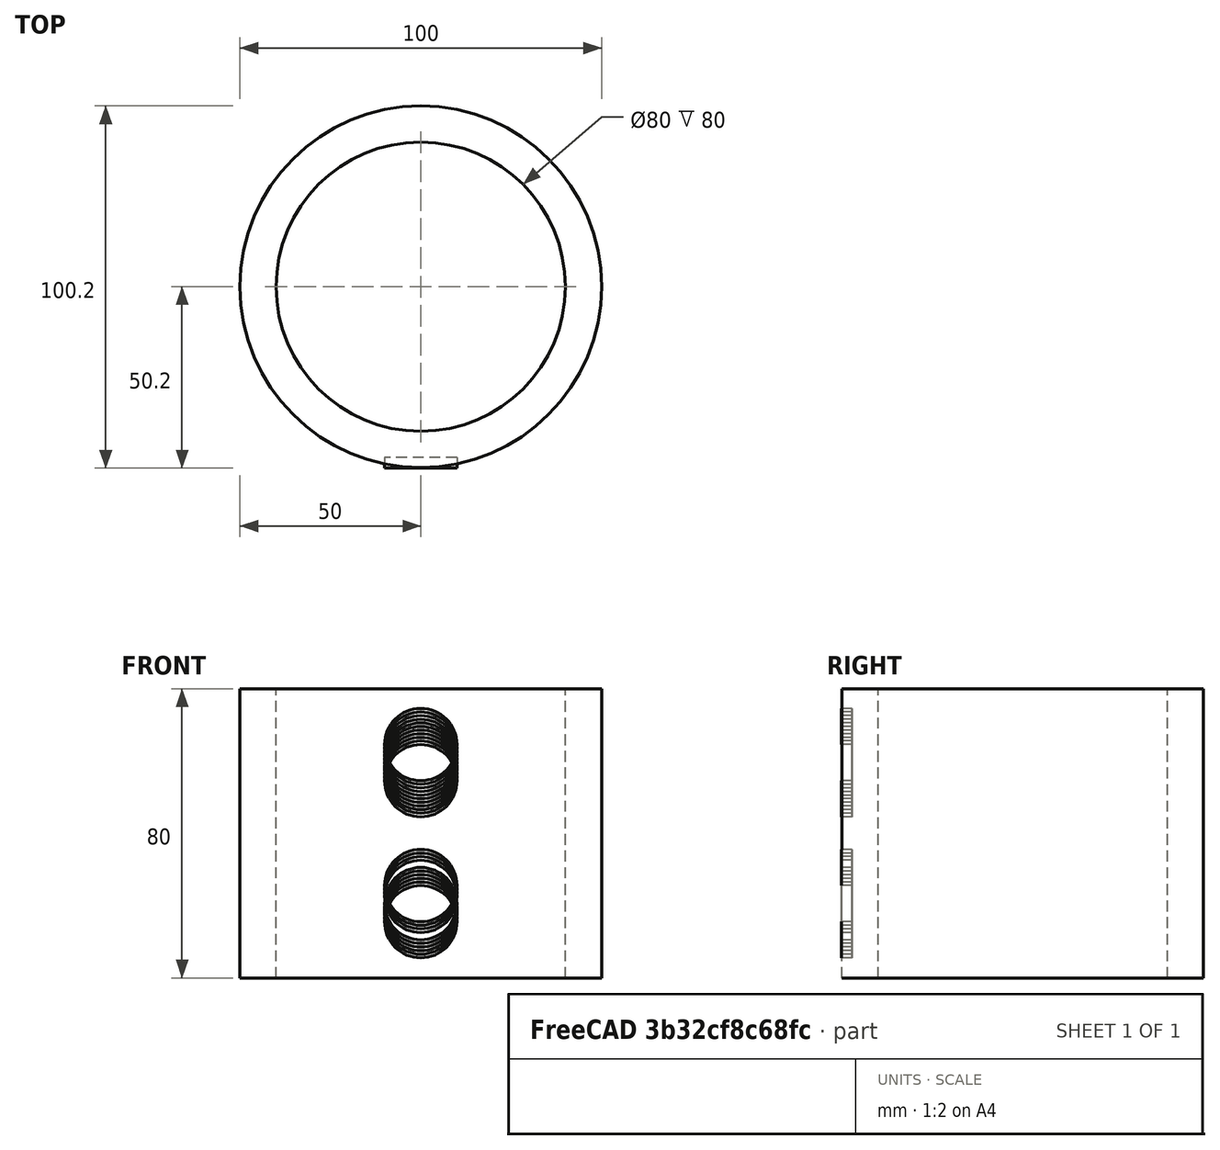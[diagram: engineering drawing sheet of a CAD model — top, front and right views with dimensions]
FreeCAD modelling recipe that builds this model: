
FCSTD DOCUMENT  (FreeCAD 0.18R16146 (Git))
Label: energy-free
License: All rights reserved
LicenseURL: http://en.wikipedia.org/wiki/All_rights_reserved
objects: Part::Cylinder×26, App::Part×13, Part::Cut×1
note: 27 computed .brp shape members not serialized (recipe doc carries the construction recipe); baked Part::Feature solids carry a one-line shape summary decoded from their .brp

FEATURE [Part::Cylinder] Cylinder  label="cercle  externe"
  Angle = 360
  AttacherType = Attacher::AttachEngine3D
  Height = 80
  Radius = 50
FEATURE [Part::Cylinder] Cylinder001  label="cercle interne"
  Angle = 360
  AttacherType = Attacher::AttachEngine3D
  Height = 80
  Radius = 40
FEATURE [Part::Cut] Cut
  Base = -> Cylinder
  Tool = -> Cylinder001
FEATURE [App::Part] Part
  Group = -> [Cylinder,Cylinder001,Cut]
  Origin = -> Origin
FEATURE [Part::Cylinder] Cylinder004  label="Cylindre004"
  Angle = 360
  AttacherType = Attacher::AttachEngine3D
  Height = 3
  Placement = pos=(0,-47.2044,15.5529) rot=(1,0,0;1.5708rad)
  Radius = 10
FEATURE [Part::Cylinder] Cylinder006  label="Cylindre006"
  Angle = 360
  AttacherType = Attacher::AttachEngine3D
  Height = 3
  Placement = pos=(0,-47.2044,64.5529) rot=(1,0,0;1.5708rad)
  Radius = 10
FEATURE [App::Part] Part001
  Group = -> [Cylinder004,Cylinder006]
  Origin = -> Origin001
  Placement = pos=(0,0,0) rot=(0,0,1;0.523599rad)
FEATURE [Part::Cylinder] Cylinder007  label="Cylindre007"
  Angle = 360
  AttacherType = Attacher::AttachEngine3D
  Height = 3
  Placement = pos=(0,-47.2044,16.5529) rot=(1,0,0;1.5708rad)
  Radius = 10
FEATURE [Part::Cylinder] Cylinder008  label="Cylindre008"
  Angle = 360
  AttacherType = Attacher::AttachEngine3D
  Height = 3
  Placement = pos=(0,-47.2044,63.5529) rot=(1,0,0;1.5708rad)
  Radius = 10
FEATURE [App::Part] Part002
  Group = -> [Cylinder007,Cylinder008]
  Origin = -> Origin002
  Placement = pos=(0,0,0) rot=(0,0,1;1.0472rad)
FEATURE [Part::Cylinder] Cylinder009  label="Cylindre009"
  Angle = 360
  AttacherType = Attacher::AttachEngine3D
  Height = 3
  Placement = pos=(0,-47.2044,17.5529) rot=(1,0,0;1.5708rad)
  Radius = 10
FEATURE [Part::Cylinder] Cylinder010  label="Cylindre010"
  Angle = 360
  AttacherType = Attacher::AttachEngine3D
  Height = 3
  Placement = pos=(0,-47.2044,62.5529) rot=(1,0,0;1.5708rad)
  Radius = 10
FEATURE [App::Part] Part003
  Group = -> [Cylinder009,Cylinder010]
  Origin = -> Origin003
  Placement = pos=(0,0,0) rot=(0,0,1;1.5708rad)
FEATURE [Part::Cylinder] Cylinder011  label="Cylindre011"
  Angle = 360
  AttacherType = Attacher::AttachEngine3D
  Height = 3
  Placement = pos=(0,-47.2044,61.5529) rot=(1,0,0;1.5708rad)
  Radius = 10
FEATURE [Part::Cylinder] Cylinder012  label="Cylindre012"
  Angle = 360
  AttacherType = Attacher::AttachEngine3D
  Height = 3
  Placement = pos=(0,-47.2044,18.5529) rot=(1,0,0;1.5708rad)
  Radius = 10
FEATURE [App::Part] Part004
  Group = -> [Cylinder012,Cylinder011]
  Origin = -> Origin004
  Placement = pos=(0,0,0) rot=(0,0,1;2.0944rad)
FEATURE [Part::Cylinder] Cylinder013  label="Cylindre013"
  Angle = 360
  AttacherType = Attacher::AttachEngine3D
  Height = 3
  Placement = pos=(0,-47.2044,19.5529) rot=(1,0,0;1.5708rad)
  Radius = 10
FEATURE [Part::Cylinder] Cylinder014  label="Cylindre014"
  Angle = 360
  AttacherType = Attacher::AttachEngine3D
  Height = 3
  Placement = pos=(0,-47.2044,60.5529) rot=(1,0,0;1.5708rad)
  Radius = 10
FEATURE [App::Part] Part005
  Group = -> [Cylinder013,Cylinder014]
  Origin = -> Origin005
  Placement = pos=(0,0,0) rot=(0,0,1;2.61799rad)
FEATURE [Part::Cylinder] Cylinder015  label="Cylindre015"
  Angle = 360
  AttacherType = Attacher::AttachEngine3D
  Height = 3
  Placement = pos=(0,-47.2044,59.5529) rot=(1,0,0;1.5708rad)
  Radius = 10
FEATURE [Part::Cylinder] Cylinder016  label="Cylindre016"
  Angle = 360
  AttacherType = Attacher::AttachEngine3D
  Height = 3
  Placement = pos=(0,-47.2044,20.5529) rot=(1,0,0;1.5708rad)
  Radius = 10
FEATURE [App::Part] Part006
  Group = -> [Cylinder016,Cylinder015]
  Origin = -> Origin006
  Placement = pos=(0,0,0) rot=(0,0,1;3.14159rad)
FEATURE [Part::Cylinder] Cylinder017  label="Cylindre017"
  Angle = 360
  AttacherType = Attacher::AttachEngine3D
  Height = 3
  Placement = pos=(0,-47.2044,58.5529) rot=(1,0,0;1.5708rad)
  Radius = 10
FEATURE [Part::Cylinder] Cylinder018  label="Cylindre018"
  Angle = 360
  AttacherType = Attacher::AttachEngine3D
  Height = 3
  Placement = pos=(0,-47.2044,22.5529) rot=(1,0,0;1.5708rad)
  Radius = 10
FEATURE [App::Part] Part007
  Group = -> [Cylinder018,Cylinder017]
  Origin = -> Origin007
  Placement = pos=(0,0,0) rot=(0,0,1;3.66519rad)
FEATURE [Part::Cylinder] Cylinder019  label="Cylindre019"
  Angle = 360
  AttacherType = Attacher::AttachEngine3D
  Height = 3
  Placement = pos=(0,-47.2044,22.5529) rot=(1,0,0;1.5708rad)
  Radius = 10
FEATURE [Part::Cylinder] Cylinder020  label="Cylindre020"
  Angle = 360
  AttacherType = Attacher::AttachEngine3D
  Height = 3
  Placement = pos=(0,-47.2044,57.5529) rot=(1,0,0;1.5708rad)
  Radius = 10
FEATURE [App::Part] Part008
  Group = -> [Cylinder019,Cylinder020]
  Origin = -> Origin008
  Placement = pos=(0,0,0) rot=(0,0,1;4.18879rad)
FEATURE [Part::Cylinder] Cylinder021  label="Cylindre021"
  Angle = 360
  AttacherType = Attacher::AttachEngine3D
  Height = 3
  Placement = pos=(0,-47.2044,23.5529) rot=(1,0,0;1.5708rad)
  Radius = 10
FEATURE [Part::Cylinder] Cylinder022  label="Cylindre022"
  Angle = 360
  AttacherType = Attacher::AttachEngine3D
  Height = 3
  Placement = pos=(0,-47.2044,56.5529) rot=(1,0,0;1.5708rad)
  Radius = 10
FEATURE [App::Part] Part009
  Group = -> [Cylinder021,Cylinder022]
  Origin = -> Origin009
  Placement = pos=(0,0,0) rot=(0,0,1;4.71239rad)
FEATURE [Part::Cylinder] Cylinder023  label="Cylindre023"
  Angle = 360
  AttacherType = Attacher::AttachEngine3D
  Height = 3
  Placement = pos=(0,-47.2044,24.5529) rot=(1,0,0;1.5708rad)
  Radius = 10
FEATURE [Part::Cylinder] Cylinder024  label="Cylindre024"
  Angle = 360
  AttacherType = Attacher::AttachEngine3D
  Height = 3
  Placement = pos=(0,-47.2044,55.5529) rot=(1,0,0;1.5708rad)
  Radius = 10
FEATURE [App::Part] Part010
  Group = -> [Cylinder023,Cylinder024]
  Origin = -> Origin010
  Placement = pos=(0,0,0) rot=(0,0,1;5.23599rad)
FEATURE [Part::Cylinder] Cylinder025  label="Cylindre025"
  Angle = 360
  AttacherType = Attacher::AttachEngine3D
  Height = 3
  Placement = pos=(0,-47.2044,54.5529) rot=(1,0,0;1.5708rad)
  Radius = 10
FEATURE [Part::Cylinder] Cylinder026  label="Cylindre026"
  Angle = 360
  AttacherType = Attacher::AttachEngine3D
  Height = 3
  Placement = pos=(0,-47.2044,25.5529) rot=(1,0,0;1.5708rad)
  Radius = 10
FEATURE [App::Part] Part011
  Group = -> [Cylinder026,Cylinder025]
  Origin = -> Origin011
  Placement = pos=(0,0,0) rot=(0,0,1;5.75959rad)
FEATURE [Part::Cylinder] Cylinder027  label="Cylindre027"
  Angle = 360
  AttacherType = Attacher::AttachEngine3D
  Height = 3
  Placement = pos=(0,-47.2044,15.5529) rot=(1,0,0;1.5708rad)
  Radius = 10
FEATURE [Part::Cylinder] Cylinder029  label="Cylindre029"
  Angle = 360
  AttacherType = Attacher::AttachEngine3D
  Height = 3
  Placement = pos=(0,-47.2044,64.5529) rot=(1,0,0;1.5708rad)
  Radius = 10
FEATURE [App::Part] Part012  label="Part000"
  Group = -> [Cylinder027,Cylinder029]
  Origin = -> Origin012
